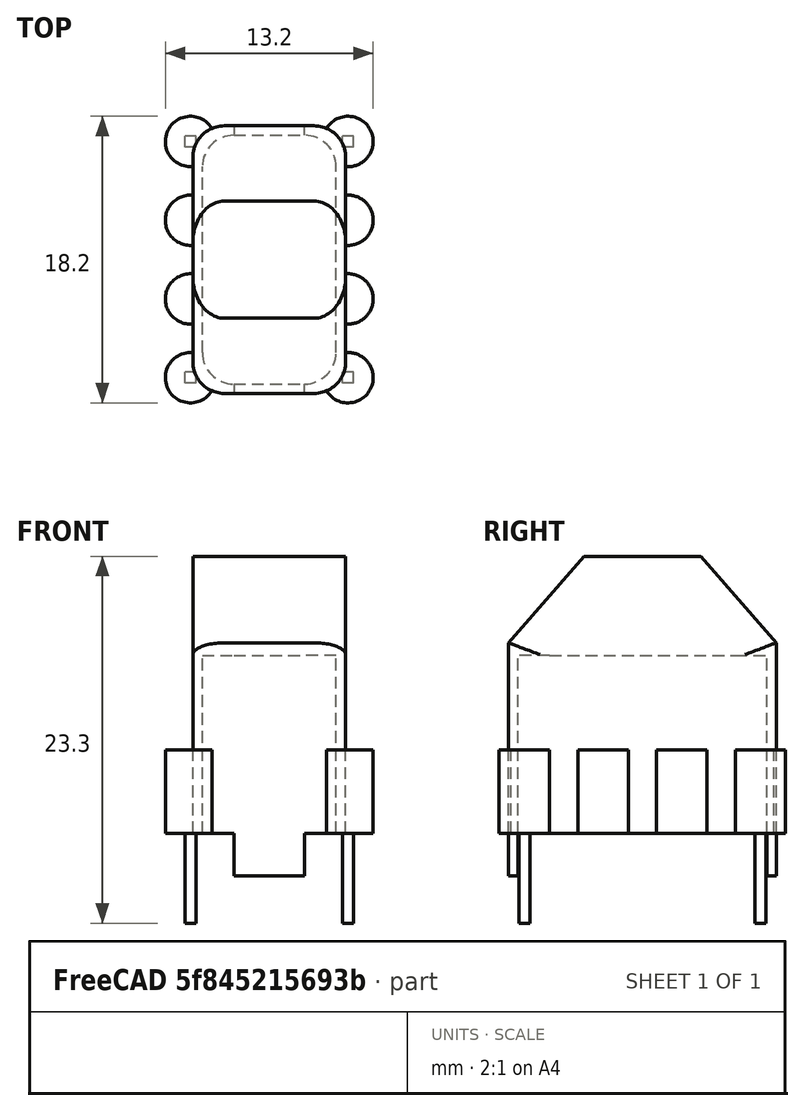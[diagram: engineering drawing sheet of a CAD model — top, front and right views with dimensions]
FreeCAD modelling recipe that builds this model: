
FCSTD DOCUMENT
Label: B82721K
objects: Part::Box×10, Part::Cylinder×8, Part::MultiFuse×6, Part::Cut×2, Part::Fillet×2
note: 28 computed .brp shape members not serialized (recipe doc carries the construction recipe); baked Part::Feature solids carry a one-line shape summary decoded from their .brp

FEATURE [Part::Box] Box001
  Height = 20.3
  Length = 9.7
  Width = 17
FEATURE [Part::Box] Box002
  Height = 10
  Length = 10
  Placement = pos=(0,17.7,14) rot=(1,0,0;0.715584rad)
  Width = 10
FEATURE [Part::Box] Box003
  Height = 10
  Length = 10
  Placement = pos=(10,-0.7,14) rot=(0,0.350207,0.936672;3.14159rad)
  Width = 10
FEATURE [Part::MultiFuse] Fusion
  Shapes = -> [Box002,Box003]
FEATURE [Part::Cut] Cut
  Base = -> Box001
  Tool = -> Fusion
FEATURE [Part::Fillet] Fillet  label="Grundkoerper"
  Base = -> Cut
  Edges = 8 edges r=2: [Edge5,Edge6,Edge8,Edge9,Edge10,Edge12,Edge13,Edge15]
  Placement = pos=(-4.85,-8.5,0) rot=(0,0,1;0rad)
FEATURE [Part::Cylinder] Cylinder
  Angle = 360
  Height = 8
  Placement = pos=(-5,7.5,0) rot=(0,0,1;0rad)
  Radius = 1.6
FEATURE [Part::Box] Box004  label="Pin"
  Height = 6
  Length = 0.7
  Placement = pos=(4.65,7.15,-3) rot=(0,0,1;0rad)
  Width = 0.7
FEATURE [Part::Box] Box005  label="Pin001"
  Height = 6
  Length = 0.7
  Placement = pos=(-5.35,7.15,-3) rot=(0,0,1;0rad)
  Width = 0.7
FEATURE [Part::Box] Box006  label="Pin002"
  Height = 6
  Length = 0.7
  Placement = pos=(-5.35,-7.85,-3) rot=(0,0,1;0rad)
  Width = 0.7
FEATURE [Part::Box] Box007  label="Pin003"
  Height = 6
  Length = 0.7
  Placement = pos=(4.65,-7.85,-3) rot=(0,0,1;0rad)
  Width = 0.7
FEATURE [Part::Cylinder] Cylinder001
  Angle = 360
  Height = 8
  Placement = pos=(-5,2.5,0) rot=(0,0,1;0rad)
  Radius = 1.6
FEATURE [Part::Cylinder] Cylinder002
  Angle = 360
  Height = 8
  Placement = pos=(-5,-2.5,0) rot=(0,0,1;0rad)
  Radius = 1.6
FEATURE [Part::Cylinder] Cylinder003
  Angle = 360
  Height = 8
  Placement = pos=(-5,-7.5,0) rot=(0,0,1;0rad)
  Radius = 1.6
FEATURE [Part::Cylinder] Cylinder004
  Angle = 360
  Height = 8
  Placement = pos=(5,7.5,0) rot=(0,0,1;0rad)
  Radius = 1.6
FEATURE [Part::Cylinder] Cylinder005
  Angle = 360
  Height = 8
  Placement = pos=(5,2.5,0) rot=(0,0,1;0rad)
  Radius = 1.6
FEATURE [Part::Cylinder] Cylinder006
  Angle = 360
  Height = 8
  Placement = pos=(5,-2.5,0) rot=(0,0,1;0rad)
  Radius = 1.6
FEATURE [Part::Cylinder] Cylinder007
  Angle = 360
  Height = 8
  Placement = pos=(5,-7.5,0) rot=(0,0,1;0rad)
  Radius = 1.6
FEATURE [Part::MultiFuse] Fusion001  label="pinholder"
  Shapes = -> [Cylinder,Cylinder001,Cylinder002,Cylinder003,Cylinder004,Cylinder005,Cylinder006,Cylinder007]
FEATURE [Part::MultiFuse] Fusion002
  Shapes = -> [Fillet,Fusion001]
FEATURE [Part::MultiFuse] Fusion003  label="Pins"
  Shapes = -> [Box004,Box005,Box006,Box007]
FEATURE [Part::Box] Box008
  Height = 2.7
  Length = 10
  Placement = pos=(2.25,-13,0) rot=(0,0,1;0rad)
  Width = 26
FEATURE [Part::Box] Box009
  Height = 2.7
  Length = 10
  Placement = pos=(-2.25,13,0) rot=(0,0,1;3.14159rad)
  Width = 26
FEATURE [Part::Box] Box010
  Height = 14
  Length = 8.5
  Placement = pos=(-4.25,-7.9,0) rot=(0,0,1;0rad)
  Width = 15.8
FEATURE [Part::Fillet] Fillet001
  Base = -> Box010
  Edges = 4 edges r=2: [Edge1,Edge3,Edge5,Edge7]
FEATURE [Part::MultiFuse] Fusion004
  Shapes = -> [Box008,Box009,Fillet001]
FEATURE [Part::Cut] Cut001  label="Koerper"
  Base = -> Fusion002
  Tool = -> Fusion004
FEATURE [Part::MultiFuse] Fusion005  label="B82721K"
  Shapes = -> [Cut001,Fusion003]
